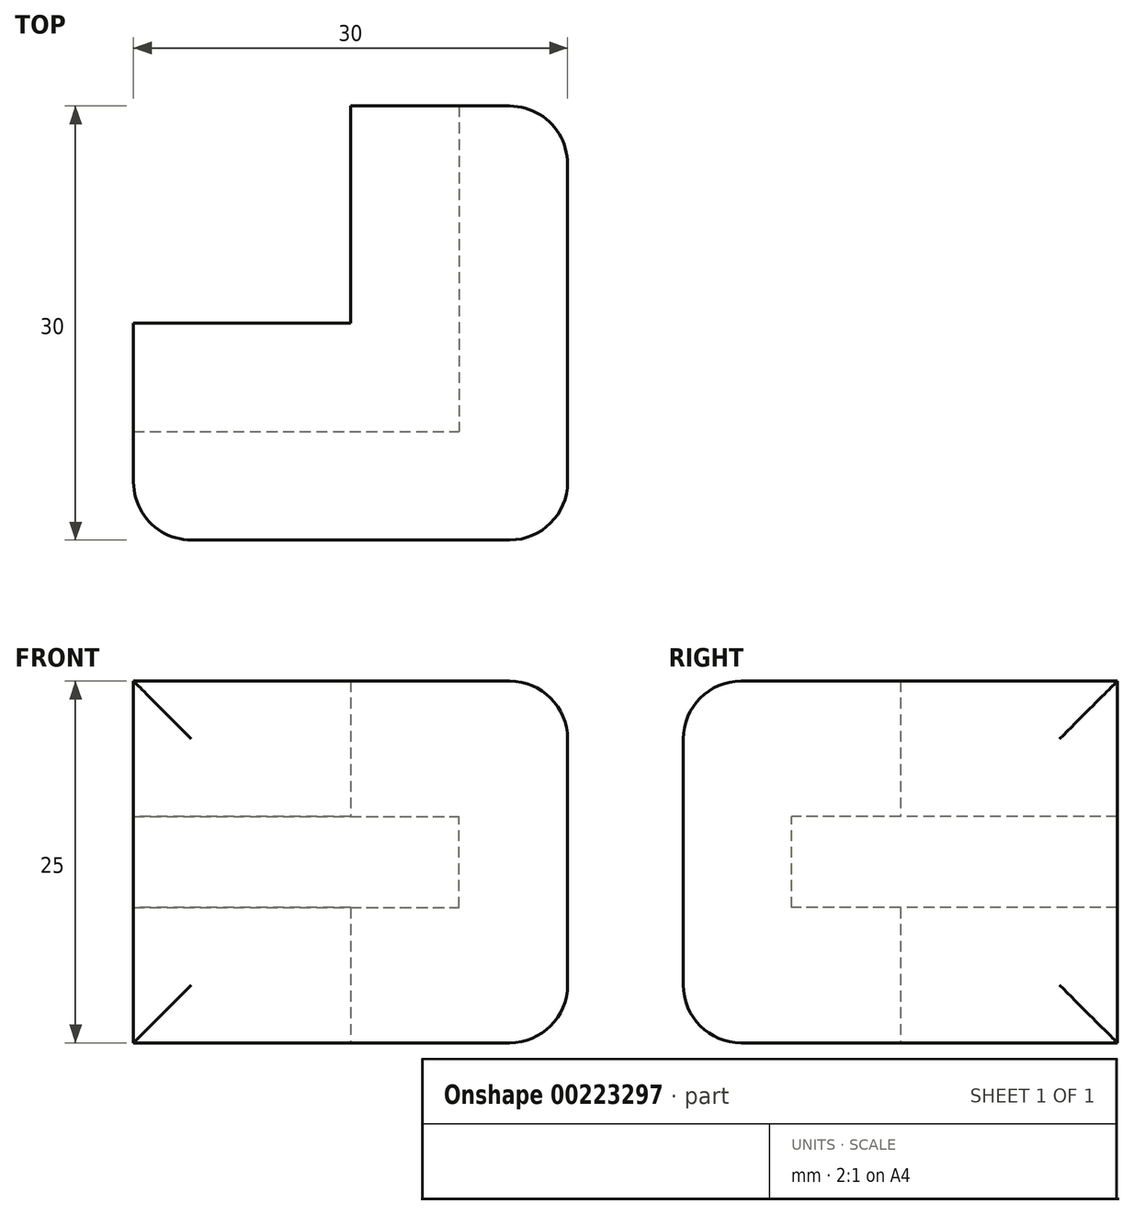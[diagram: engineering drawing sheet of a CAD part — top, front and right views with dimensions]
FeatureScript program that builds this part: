
annotation { "Feature Type Name" : "Feature", "Feature Type Description" : "" }
export const myFeature = defineFeature(function(context is Context, id is Id, definition is map)
    precondition{}
    {
        {
            var Q0;
            Q0=qCreatedBy(makeId("Top.planeOp"),FACE);
            var sketch = newSketch(context, id + "F0", { "sketchPlane" : qUnion([Q0])});
            skLineSegment(sketch, "E0.bottom", {"start": v(0, 15) * mm, "end": v(15, 15) * mm});
            skLineSegment(sketch, "E0.top", {"start": v(-15, -15) * mm, "end": v(15, -15) * mm});
            skLineSegment(sketch, "E0.left", {"start": v(-15, 0) * mm, "end": v(-15, -15) * mm});
            skLineSegment(sketch, "E0.right", {"start": v(15, 15) * mm, "end": v(15, -15) * mm});
            skLineSegment(sketch, "E1", {"start": v(0, 15) * mm, "end": v(0, 0) * mm});
            skLineSegment(sketch, "E2", {"start": v(0, 0) * mm, "end": v(-15, 0) * mm});
            skSolve(sketch);
        }
        {
            var Q0;
            Q0=makeQuery(id+"F0.imprint","IMPRINT",FACE,{"disambiguationData":[TD([[makeQuery(id+"F0.imprint","IMPRINT",EDGE,{"derivedFrom":sQuery(id+"F0.wireOp",EDGE,"E0.bottom")}),-1.0]])]});
            extrude(context, id + "F1", {"entities" : qUnion([Q0]), "endBound" : BoundingType.SYMMETRIC, "depth" : 25 * mm});
        }
        {
            var Q0;
            Q0=qCreatedBy(makeId("Top.planeOp"),FACE);
            var sketch = newSketch(context, id + "F2", { "sketchPlane" : qUnion([Q0])});
            skLineSegment(sketch, "E3.1", {"start": v(0, 15) * mm, "end": v(0, 0) * mm});
            skLineSegment(sketch, "E3.3", {"start": v(0, 15) * mm, "end": v(7.5, 15) * mm});
            skLineSegment(sketch, "E3.5", {"start": v(-15, 0) * mm, "end": v(-15, -7.5) * mm});
            skLineSegment(sketch, "E3.6", {"start": v(0, 0) * mm, "end": v(-15, 0) * mm});
            skPoint(sketch, "E3.4.end.orphan", {"position": v(15, -15) * mm});
            skPoint(sketch, "E3.14.end.orphan", {"position": v(15, -15) * mm});
            skPoint(sketch, "E3.15.end.orphan", {"position": v(-15, -15) * mm});
            skPoint(sketch, "E3.17.end.orphan", {"position": v(-15, 0) * mm});
            skPoint(sketch, "E3.13.end.orphan", {"position": v(0, 0) * mm});
            skPoint(sketch, "E3.10.end.orphan", {"position": v(15, 15) * mm});
            skPoint(sketch, "E3.10.start.orphan", {"position": v(0, 15) * mm});
            skLineSegment(sketch, "E4", {"start": v(-15, -7.5) * mm, "end": v(7.5, -7.5) * mm});
            skLineSegment(sketch, "E5", {"start": v(7.5, 15) * mm, "end": v(7.5, -7.5) * mm});
            skSolve(sketch);
        }
        {
            var Q0;
            Q0 = qSketchRegion(id + "F2", true);
            extrude(context, id + "F3", {"entities" : qUnion([Q0]), "operationType" : NewBodyOperationType.REMOVE, "endBound" : BoundingType.SYMMETRIC, "oppositeDirection" : true, "depth" : 6.3 * mm});
        }
        {
            var Q0;
            Q0=makeQuery(id+"F1.opExtrude","SWEPT_EDGE",EDGE,{"disambiguationData":[OSD([sQuery(id+"F0.wireOp",EDGE,"E0.top"),sQuery(id+"F0.wireOp",EDGE,"E0.left")])]});
            var Q1;
            Q1=makeQuery(id+"F1.opExtrude","SWEPT_EDGE",EDGE,{"disambiguationData":[OSD([sQuery(id+"F0.wireOp",EDGE,"E0.top"),sQuery(id+"F0.wireOp",EDGE,"E0.right")])]});
            var Q2;
            Q2=makeQuery(id+"F1.opExtrude","SWEPT_EDGE",EDGE,{"disambiguationData":[OSD([sQuery(id+"F0.wireOp",EDGE,"E0.bottom"),sQuery(id+"F0.wireOp",EDGE,"E0.right")])]});
            var Q3;
            Q3=makeQuery(id+"F1.opExtrude","CAP_EDGE",EDGE,{"disambiguationData":[OSD([sQuery(id+"F0.wireOp",EDGE,"E0.right")])],"isStart":false});
            var Q4;
            Q4=makeQuery(id+"F1.opExtrude","CAP_EDGE",EDGE,{"disambiguationData":[OSD([sQuery(id+"F0.wireOp",EDGE,"E0.top")])],"isStart":false});
            var Q5;
            Q5=makeQuery(id+"F1.opExtrude","CAP_EDGE",EDGE,{"disambiguationData":[OSD([sQuery(id+"F0.wireOp",EDGE,"E0.right")])],"isStart":true});
            var Q6;
            Q6=makeQuery(id+"F1.opExtrude","CAP_EDGE",EDGE,{"disambiguationData":[OSD([sQuery(id+"F0.wireOp",EDGE,"E0.top")])],"isStart":true});
            fillet(context, id + "F4", {"entities" : qUnion([Q0, Q1, Q2, Q3, Q4, Q5, Q6]), "radius" : 4 * mm, "tangentPropagation" : true, "allowEdgeOverflow" : false});
        }
    });
